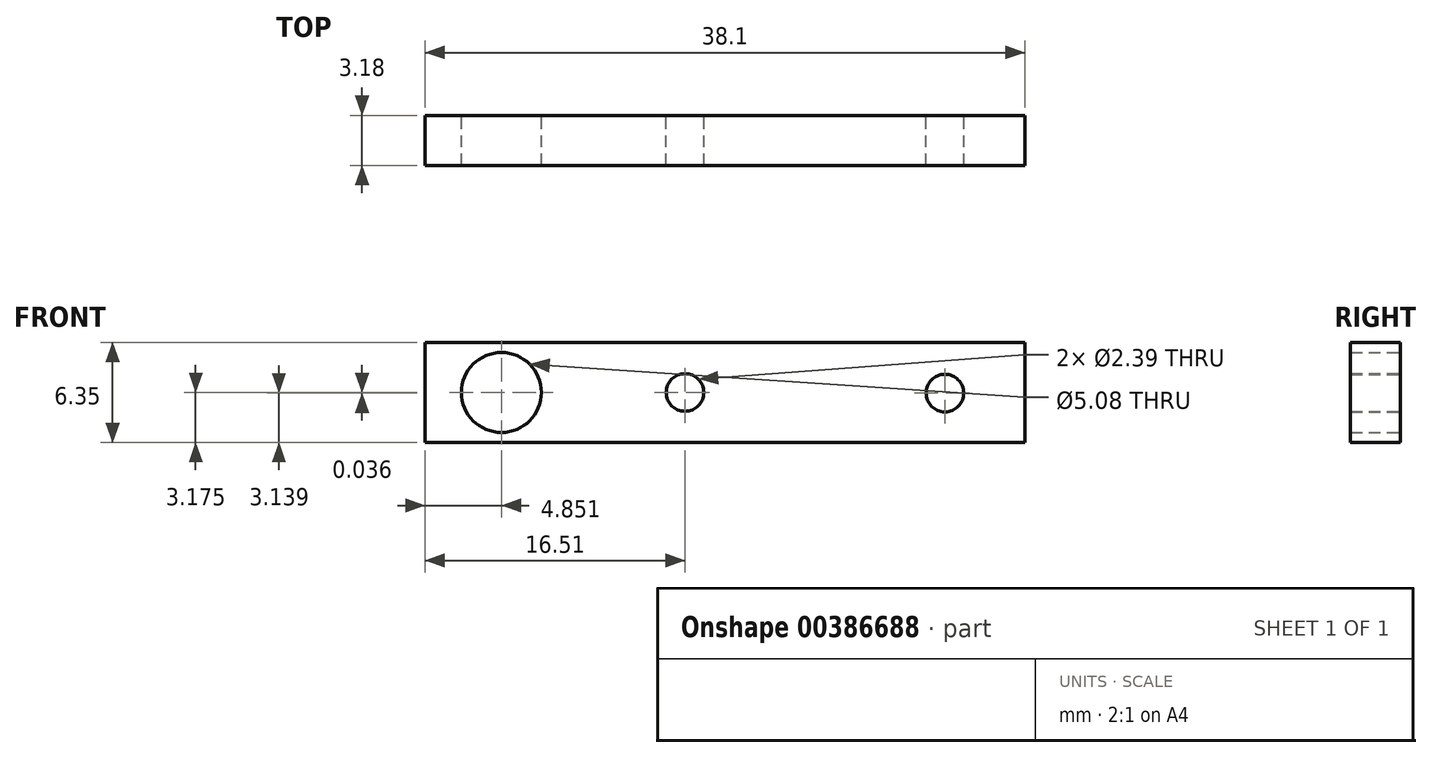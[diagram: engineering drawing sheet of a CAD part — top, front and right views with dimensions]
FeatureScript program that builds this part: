
annotation { "Feature Type Name" : "Feature", "Feature Type Description" : "" }
export const myFeature = defineFeature(function(context is Context, id is Id, definition is map)
    precondition{}
    {
        {
            var Q0;
            Q0=qCreatedBy(makeId("Front.planeOp"),FACE);
            var sketch = newSketch(context, id + "F0", { "sketchPlane" : qUnion([Q0])});
            skLineSegment(sketch, "E0.bottom", {"start": v(0, 0) * mm, "end": v(38.1, 0) * mm});
            skLineSegment(sketch, "E0.top", {"start": v(0, 6.35) * mm, "end": v(38.1, 6.35) * mm});
            skLineSegment(sketch, "E0.left", {"start": v(0, 0) * mm, "end": v(0, 6.35) * mm});
            skLineSegment(sketch, "E0.right", {"start": v(38.1, 0) * mm, "end": v(38.1, 6.35) * mm});
            skCircle(sketch, "E1", {"center": v(4.85, 3.18) * mm, "radius": 2.54 * mm});
            skLineSegment(sketch, "E2", {"start": v(16.34, 3.18) * mm, "end": v(16.51, 3.18) * mm});
            skCircle(sketch, "E3", {"center": v(16.51, 3.18) * mm, "radius": 1.2 * mm});
            skCircle(sketch, "E4", {"center": v(33.02, 3.14) * mm, "radius": 1.2 * mm});
            skSolve(sketch);
        }
        {
            var Q0;
            Q0 = qSketchRegion(id + "F0", true);
            extrude(context, id + "F1", {"entities" : qUnion([Q0]), "depth" : 3.17 * mm});
        }
    });
